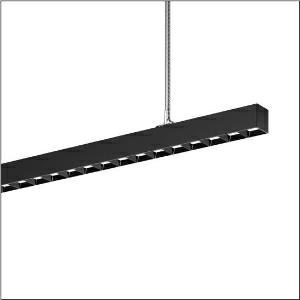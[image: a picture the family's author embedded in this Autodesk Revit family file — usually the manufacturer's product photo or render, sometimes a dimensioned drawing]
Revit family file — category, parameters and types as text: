
# Revit family: silica_r__21_51mx32dc4dbb_b922
name_source: partatom
category: Lighting Fixtures
units: mm (PartAtom-declared; Revit-internal decimal feet)

## family parameters
Cut with Voids When Loaded = No
Host = Face
Light Source = No
Part Type = Normal
Room Calculation Point = No
Round Connector Dimension = Use Diameter
Shared = No

## types (1)
- --- (1 x LED, 18230 lm, 105.8 W, 4000K)
    Apparent Load = 106 VA
    CIE Flux Codes = 86 99 100 59 100
    Color Rendering = 80
    Color Temperature = 4000K
    Default Elevation = 1800 mm
    Description = Silica® 21, office luminaire, primary light control with darklight reflector, of PMMA, black, CAT 2 (L<= 3000cd/m²), light emission: direct/indirect distribution, primary light characteristic: symmetric, installation type: suspended mounting, LED, rated luminous flux: 18.230lm, luminous efficacy: 172lm/W, light colour: 840, colour temperature: 4000K, with terminal, 3+2-pole, max. 2.5mm², mains connection: 220..240V, AC, 50/60Hz, rated input power: 105.8W, luminaire housing, of aluminium, jet black (RAL 9005), length: 3.004mm, width: 53mm, height: 53mm, protection rating (complete): IP20, insulation class (complete): insulation class I (protective earthing), certification: CE, permissible operating ambient temperature: 0..+35°C, standard: EN 50419, packaging unit: 1 piece
    Height = 53 mm
    Lamp = 1 x LED
    Lamp Light Flux = 18230 lm
    Lamp Power = 105.8 W
    Lamp count = 1
    Length = 3004 mm
    Luminous efficacy = 172 lm/W
    Manufacturer = Siteco
    ModVariant = No
    Model = 51MX32DC4DBB
    Mounting Place = Ceiling
    Mounting Type = Pendant
    Number of Poles = 1
    OnlyDefault = Yes
    Power Factor = 1
    Product Name = Silica® 21
    Product group = office luminaire | ceiling pendant
    ProductGroupID = 902
    Protection Class = Protection class I
    Protection Degree = IP 20
    RLX_Detail_Level = 1
    RLX_Emergency_Light_Flux = 0 lm
    RLX_Emergency_Type = 0
    RLX_Emergency_Type_DB = No
    RlxData = <blob elided: 66733 chars, md5=92d733dc>
    Socket = socket
    Standby Power = 0 W
    System Light Flux = 18230 lm
    System Power = 106 W
    Type Comments = factory setting: luminous flux: 100 % | dim-lin: 254 | 366 mA
    Type Image = l_1297774.jpg
    URL = http://relux.com
    VarID = @adj_052805
    Voltage = 0 V
    Weight = 0.00 kg
    Width = 53 mm

## geometry (parser evidence)
native form markers: Blend x4, Sweep x13
no freeform markers — native parametric forms only
